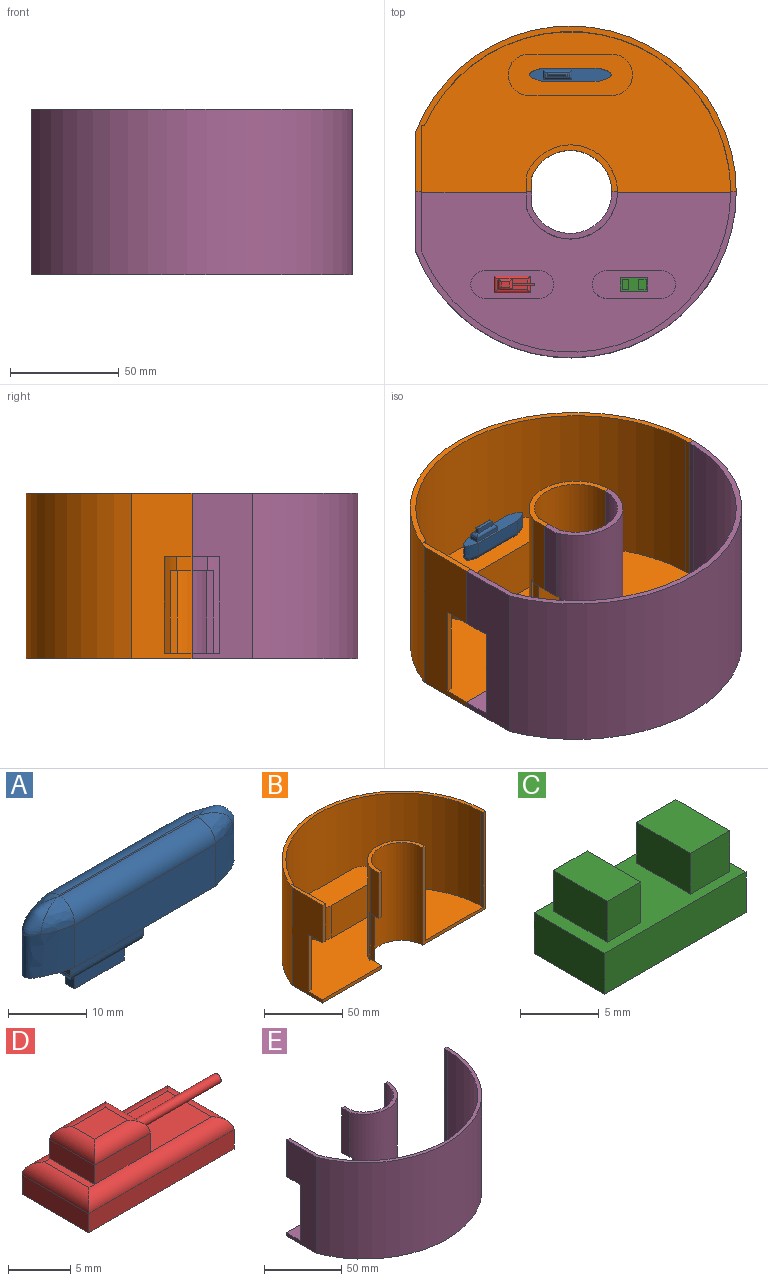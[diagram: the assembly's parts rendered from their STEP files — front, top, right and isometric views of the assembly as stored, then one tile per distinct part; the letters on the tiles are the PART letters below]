
ASSEMBLY  parts=5 mates=4
PART A: 32 faces, bbox 42x6.8x15.9 mm
  f0: plane 42.02x6.16mm, normal (0,0,-1), area 151.4mm2, adj f1,f2,f3,f4,f14,f15,f16,f17
  f1: extruded ~6.58x6.16mm, area 93mm2, adj f0,f2,f4,f6,f7,f9
  f2: plane 25.4x6.58mm, normal (0,-1,0), area 167.2mm2, adj f0,f1,f3,f8
  f3: extruded ~6.58x6.16mm, area 92.6mm2, adj f0,f2,f4,f10,f12,f13
  f4: plane 25.4x6.58mm, normal (0,1,0), area 167.2mm2, adj f0,f1,f3,f11
  f5: plane 25.67x0.28mm, normal (0,0,1), area 6.9mm2, adj f6,f8,f9,f10,f11,f13
  f6: bspline ~6.05x4.39mm, area 15.2mm2, adj f1,f5,f7,f8
  f7: bspline ~5.92x3.06mm, area 15.5mm2, adj f1,f6,f9
  f8: cylinder r=2.94mm len=25.4mm, axis (-1,0,0), area 115.7mm2, adj f2,f5,f6,f10
  f9: bspline ~5.92x4.35mm, area 15.1mm2, adj f1,f5,f7,f11
  f10: bspline ~5.89x4.34mm, area 15mm2, adj f3,f5,f8,f12
  f11: cylinder r=2.94mm len=25.4mm, axis (1,0,0), area 115.7mm2, adj f4,f5,f9,f13
  f12: bspline ~5.89x3.07mm, area 11.3mm2, adj f3,f10,f13
  f13: bspline ~7.54x4.77mm, area 15.1mm2, adj f3,f5,f11,f12
  f14: plane 4.16x1.91mm, normal (-1,0,0), area 7.9mm2, adj f0,f15,f17,f28
  f15: plane 13.17x1.91mm, normal (0,1,0), area 25.1mm2, adj f0,f14,f16,f30
  f16: plane 4.16x1.91mm, normal (1,0,0), area 7.9mm2, adj f0,f15,f17,f31
  f17: plane 13.17x1.91mm, normal (0,-1,0), area 25.1mm2, adj f0,f14,f16,f29
  f18: plane 10.63x1.62mm, normal (0,0,-1), area 2.9mm2, adj f19,f21,f22,f28,f29,f30,f31
  f19: plane 2.41x1.64mm, normal (-1,0,0), area 4mm2, adj f18,f20,f22,f24,f30
  f20: plane 9.02x2.41mm, normal (0,1,0), area 21.8mm2, adj f19,f21,f26,f30
  f21: plane 2.41x1.64mm, normal (1,0,0), area 4mm2, adj f18,f20,f22,f27,f30
  f22: plane 9.02x2.41mm, normal (0,-1,0), area 21.8mm2, adj f18,f19,f21,f25
  f23: plane 7.49x0.12mm, normal (0,0,-1), area 0.9mm2, adj f24,f25,f26,f27
  f24: plane 1.64x0.76mm, normal (-0.71,0,-0.71), area 0.9mm2, adj f19,f23,f25,f26
  f25: plane 9.02x0.76mm, normal (0,-0.71,-0.71), area 8.9mm2, adj f22,f23,f24,f27
  f26: plane 9.02x0.76mm, normal (0,0.71,-0.71), area 8.9mm2, adj f20,f23,f24,f27
  f27: plane 1.64x0.76mm, normal (0.71,0,-0.71), area 0.9mm2, adj f21,f23,f25,f26
  f28: cylinder r=1.27mm len=4.16mm, axis (0,-1,0), area 5.8mm2, adj f14,f18,f29,f30
  f29: cylinder r=1.27mm len=13.17mm, axis (1,0,0), area 23.7mm2, adj f17,f18,f28,f31
  f30: cylinder r=1.27mm len=13.17mm, axis (-1,0,0), area 23.9mm2, adj f15,f18,f19,f20,f21,f28,f31
  f31: cylinder r=1.27mm len=4.16mm, axis (0,1,0), area 5.8mm2, adj f16,f18,f29,f30
PART B: 32 faces, bbox 147.2x76.2x76.2 mm
  f0: plane 147.23x76.2mm, normal (0,0,1), area 593.9mm2, adj f2,f5,f10,f11,f12,f16,f28,f29
  f1: plane 73.66x0.15mm, normal (0,1,0), area 11mm2, adj f4,f6,f8,f31
  f2: plane 29.21x2.54mm, normal (0,-1,0), area 74.2mm2, adj f0,f12,f16,f18
  f3: plane 53.25x2.54mm, normal (0,-1,0), area 135.3mm2, adj f6,f7,f12,f15
  f4: plane 41.9x21.59mm, normal (0,0,1), area 161.9mm2, adj f1,f8,f9,f10,f13,f14,f17,f31
  f5: cylinder r=73.66mm len=140.67mm, axis (0,0,-1), area 14543.8mm2, adj f0,f6,f28,f29
  f6: plane 144.69x73.66mm, normal (0,0,1), area 6750.3mm2, adj f1,f3,f5,f7,f8,f10,f12,f16
  f7: plane 6.86x2.54mm, normal (1,0,0), area 17.4mm2, adj f3,f6,f9,f15
  f8: cylinder r=21.59mm len=73.66mm, axis (0,0,-1), area 4146.6mm2, adj f1,f4,f6,f17,f20,f21
  f9: cylinder r=19.05mm len=76.2mm, axis (0,0,-1), area 4025.6mm2, adj f4,f7,f10,f14,f15,f22
  f10: plane 76.2x57.15mm, normal (0,-1,0), area 519.4mm2, adj f0,f4,f6,f9,f11,f15,f30,f31
  f11: cylinder r=76.2mm len=147.23mm, axis (0,0,-1), area 16089.2mm2, adj f0,f10,f12,f15
  f12: plane 76.2x27.6mm, normal (-1,0,0), area 1538.8mm2, adj f0,f2,f3,f6,f11,f15,f18,f19
  f13: plane 35.56x2.54mm, normal (0,-1,0), area 90.3mm2, adj f4,f14,f17,f20
  f14: plane 35.56x6.86mm, normal (1,0,0), area 243.9mm2, adj f4,f9,f13,f20
  f15: plane 147.23x76.2mm, normal (0,0,-1), area 8460.7mm2, adj f3,f7,f9,f10,f11,f12
  f16: plane 73.66x30.48mm, normal (1,0,0), area 1680.6mm2, adj f0,f2,f6,f18,f19,f28
  f17: plane 35.56x7.32mm, normal (-1,0,0), area 260.2mm2, adj f4,f8,f13,f20
  f18: plane 12.7x2.54mm, normal (0,0,-1), area 32.3mm2, adj f2,f12,f16,f19
  f19: plane 44.45x2.54mm, normal (0,-1,0), area 112.9mm2, adj f6,f12,f16,f18
  f20: plane 10.01x2.54mm, normal (0,0,-1), area 23.9mm2, adj f8,f13,f14,f17,f21,f22
  f21: plane 38.1x1.36mm, normal (0,-1,0), area 51.7mm2, adj f6,f8,f20,f22
  f22: plane 38.1x3.15mm, normal (-1,0,0), area 120mm2, adj f6,f9,f20,f21
  f23: cylinder r=9.53mm len=25.4mm, axis (0,0,-1), area 760.1mm2, adj f6,f24,f26,f27
  f24: plane 38.1x25.4mm, normal (0,-1,0), area 967.7mm2, adj f6,f23,f25,f27
  f25: cylinder r=9.53mm len=25.4mm, axis (0,0,-1), area 760.1mm2, adj f6,f24,f26,f27
  f26: plane 38.1x25.4mm, normal (0,1,0), area 967.7mm2, adj f6,f23,f25,f27
  f27: plane 57.15x19.05mm, normal (0,0,1), area 1010.8mm2, adj f23,f24,f25,f26
  f28: plane 73.66x1.43mm, normal (0,-1,0), area 105.1mm2, adj f0,f5,f6,f16
  f29: plane 73.66x0.04mm, normal (0,-1,0), area 3.2mm2, adj f0,f5,f6,f30
  f30: plane 73.66x2.54mm, normal (-1,0,0), area 187.1mm2, adj f0,f6,f10,f29
  f31: plane 73.66x2.54mm, normal (1,0,0), area 187.1mm2, adj f1,f4,f6,f10
PART C: 16 faces, bbox 12.7x6.4x6.4 mm
  f0: plane 12.7x3.18mm, normal (0,1,0), area 40.3mm2, adj f1,f3,f4,f5
  f1: plane 6.35x3.18mm, normal (-1,0,0), area 20.2mm2, adj f0,f2,f4,f5
  f2: plane 12.7x3.18mm, normal (0,-1,0), area 40.3mm2, adj f1,f3,f4,f5
  f3: plane 6.35x3.18mm, normal (1,0,0), area 20.2mm2, adj f0,f2,f4,f5
  f4: plane 12.7x6.35mm, normal (0,0,1), area 49mm2, adj f0,f1,f2,f3,f7,f8,f9,f10
  f5: plane 12.7x6.35mm, normal (0,0,-1), area 80.6mm2, adj f0,f1,f2,f3
  f6: plane 4.83x3.03mm, normal (0,0,1), area 14.6mm2, adj f7,f8,f9,f10
  f7: plane 4.83x3.18mm, normal (1,0,0), area 15.3mm2, adj f4,f6,f8,f10
  f8: plane 3.18x3.03mm, normal (0,-1,0), area 9.6mm2, adj f4,f6,f7,f9
  f9: plane 4.83x3.18mm, normal (-1,0,0), area 15.3mm2, adj f4,f6,f8,f10
  f10: plane 3.18x3.03mm, normal (0,1,0), area 9.6mm2, adj f4,f6,f7,f9
  f11: plane 4.83x3.53mm, normal (0,0,1), area 17mm2, adj f12,f13,f14,f15
  f12: plane 4.83x3.18mm, normal (1,0,0), area 15.3mm2, adj f4,f11,f13,f15
  f13: plane 3.53x3.18mm, normal (0,-1,0), area 11.2mm2, adj f4,f11,f12,f14
  f14: plane 4.83x3.18mm, normal (-1,0,0), area 15.3mm2, adj f4,f11,f13,f15
  f15: plane 3.53x3.18mm, normal (0,1,0), area 11.2mm2, adj f4,f11,f12,f14
PART D: 22 faces, bbox 18.4x7.6x6.4 mm
  f0: plane 5.04x0.62mm, normal (0,0,1), area 3.1mm2, adj f10,f16,f17,f19
  f1: plane 16.51x1.89mm, normal (0,1,0), area 31.2mm2, adj f2,f4,f6,f16
  f2: plane 7.62x1.89mm, normal (-1,0,0), area 14.4mm2, adj f1,f3,f6,f17
  f3: plane 16.51x1.89mm, normal (0,-1,0), area 31.2mm2, adj f2,f4,f6,f19
  f4: plane 7.62x1.89mm, normal (1,0,0), area 14.4mm2, adj f1,f3,f6,f18
  f5: plane 6.97x5.04mm, normal (0,0,1), area 35.1mm2, adj f8,f16,f18,f19
  f6: plane 16.51x7.62mm, normal (0,0,-1), area 125.8mm2, adj f1,f2,f3,f4
  f7: plane 3.77x2.5mm, normal (0,0,1), area 9.5mm2, adj f12,f13,f14,f15
  f8: plane 5.08x1.89mm, normal (1,0,0), area 9mm2, adj f5,f9,f11,f14,f16,f19,f20
  f9: plane 6.35x1.89mm, normal (0,-1,0), area 12mm2, adj f8,f10,f15,f19
  f10: plane 5.08x1.89mm, normal (-1,0,0), area 9.6mm2, adj f0,f9,f11,f13,f16,f19
  f11: plane 6.35x1.89mm, normal (0,1,0), area 12mm2, adj f8,f10,f12,f16
  f12: cylinder r=1.29mm len=6.35mm, axis (1,0,0), area 11mm2, adj f7,f11,f13,f14
  f13: cylinder r=1.29mm len=5.08mm, axis (0,1,0), area 8.4mm2, adj f7,f10,f12,f15
  f14: cylinder r=1.29mm len=5.08mm, axis (0,-1,0), area 8.4mm2, adj f7,f8,f12,f15
  f15: cylinder r=1.29mm len=6.35mm, axis (-1,0,0), area 11mm2, adj f7,f9,f13,f14
  f16: cylinder r=1.29mm len=16.51mm, axis (1,0,0), area 31.4mm2, adj f0,f1,f5,f8,f10,f11,f17,f18
  f17: cylinder r=1.29mm len=7.62mm, axis (0,1,0), area 13.5mm2, adj f0,f2,f16,f19
  f18: cylinder r=1.29mm len=7.62mm, axis (0,-1,0), area 13.5mm2, adj f4,f5,f16,f19
  f19: cylinder r=1.29mm len=16.51mm, axis (-1,0,0), area 31.4mm2, adj f0,f3,f5,f8,f9,f10,f17,f18
  f20: cylinder r=0.44mm len=10.16mm, axis (-1,0,0), area 28.4mm2, adj f8,f21
  f21: plane 0.89x0.89mm, normal (1,0,0), area 0.6mm2, adj f20
PART E: 39 faces, bbox 147.2x76.2x76.2 mm
  f0: plane 41.9x21.59mm, normal (0,0,1), area 161.9mm2, adj f1,f2,f9,f10,f11,f14,f15,f37
  f1: plane 73.66x0.15mm, normal (0,-1,0), area 11mm2, adj f0,f5,f14,f37
  f2: plane 35.56x2.54mm, normal (0,1,0), area 90.3mm2, adj f0,f11,f15,f21
  f3: plane 29.21x2.54mm, normal (0,1,0), area 74.2mm2, adj f4,f8,f16,f19
  f4: plane 147.23x76.2mm, normal (0,0,1), area 596.2mm2, adj f3,f8,f9,f12,f16,f17,f36,f38
  f5: plane 144.69x73.66mm, normal (0,0,1), area 6858.7mm2, adj f1,f6,f7,f8,f9,f14,f16,f17
  f6: plane 6.86x2.54mm, normal (1,0,0), area 17.4mm2, adj f5,f7,f10,f13
  f7: plane 53.25x2.54mm, normal (0,1,0), area 135.3mm2, adj f5,f6,f8,f13
  f8: plane 76.2x27.6mm, normal (-1,0,0), area 1538.8mm2, adj f3,f4,f5,f7,f12,f13,f18,f19
  f9: plane 76.2x57.15mm, normal (0,1,0), area 519.4mm2, adj f0,f4,f5,f10,f12,f13,f36,f37
  f10: cylinder r=19.05mm len=76.2mm, axis (0,0,-1), area 4025.6mm2, adj f0,f6,f9,f11,f13,f20
  f11: plane 35.56x6.86mm, normal (1,0,0), area 243.9mm2, adj f0,f2,f10,f21
  f12: cylinder r=76.2mm len=147.23mm, axis (0,0,-1), area 16089.2mm2, adj f4,f8,f9,f13
  f13: plane 147.23x76.2mm, normal (0,0,-1), area 8460.7mm2, adj f6,f7,f8,f9,f10,f12
  f14: cylinder r=21.59mm len=73.66mm, axis (0,0,-1), area 4146.6mm2, adj f0,f1,f5,f15,f21,f22
  f15: plane 35.56x7.32mm, normal (-1,0,0), area 260.2mm2, adj f0,f2,f14,f21
  f16: plane 73.66x27.12mm, normal (1,0,0), area 1433.3mm2, adj f3,f4,f5,f17,f18,f19
  f17: cylinder r=73.66mm len=142.1mm, axis (0,0,-1), area 14812.5mm2, adj f4,f5,f16,f38
  f18: plane 44.45x2.54mm, normal (0,1,0), area 112.9mm2, adj f5,f8,f16,f19
  f19: plane 12.7x2.54mm, normal (0,0,-1), area 32.3mm2, adj f3,f8,f16,f18
  f20: plane 38.1x3.15mm, normal (-1,0,0), area 120mm2, adj f5,f10,f21,f22
  f21: plane 10.01x2.54mm, normal (0,0,-1), area 23.9mm2, adj f2,f11,f14,f15,f20,f22
  f22: plane 38.1x1.36mm, normal (0,1,0), area 51.7mm2, adj f5,f14,f20,f21
  f23: plane 25.4x25.4mm, normal (0,-1,0), area 645.1mm2, adj f5,f24,f26,f27
  f24: cylinder r=6.35mm len=25.4mm, axis (0,0,-1), area 506.7mm2, adj f5,f23,f25,f27
  f25: plane 25.4x25.4mm, normal (0,1,0), area 645.1mm2, adj f5,f24,f26,f27
  f26: cylinder r=6.35mm len=25.4mm, axis (0,0,-1), area 506.7mm2, adj f5,f23,f25,f27
  f27: plane 38.1x12.7mm, normal (0,0,1), area 449.2mm2, adj f23,f24,f25,f26
  f28: cylinder r=6.35mm len=25.4mm, axis (0,0,-1), area 509.8mm2, adj f5,f29,f34,f35
  f29: plane 25.52x25.4mm, normal (0,-1,0), area 648.3mm2, adj f5,f28,f30,f35
  f30: plane 25.4x0mm, normal (1,0,0), area 0mm2, adj f5,f29,f31,f35
  f31: cylinder r=6.35mm len=25.4mm, axis (0,0,-1), area 500.5mm2, adj f5,f30,f32,f35
  f32: plane 25.4x0mm, normal (1,0,0), area 0mm2, adj f5,f31,f33,f35
  f33: plane 25.64x25.4mm, normal (0,1,0), area 651.4mm2, adj f5,f32,f34,f35
  f34: plane 25.4x0mm, normal (-1,0,0), area 0mm2, adj f5,f28,f33,f35
  f35: plane 38.22x12.7mm, normal (0,0,1), area 450.8mm2, adj f28,f29,f30,f31,f32,f33,f34
  f36: plane 73.66x2.54mm, normal (-1,0,0), area 187.1mm2, adj f4,f5,f9,f38
  f37: plane 73.66x2.54mm, normal (1,0,0), area 187.1mm2, adj f0,f1,f5,f9
  f38: plane 73.66x0.04mm, normal (0,1,0), area 3.2mm2, adj f4,f5,f17,f36
PLACE A rot(axis=(1,0,0),180deg) t=(13.15,75.23,57.71)mm
PLACE B t=(-4.7,-0.55,20.25)mm
PLACE C t=(65.89,-81.59,48.19)mm
PLACE D t=(-7.07,-72.54,48.19)mm
PLACE E t=(-4.7,-0.55,20.25)mm
MATE fastened D.f6 <-> E.f27  axis (0,0,-1) through (-31.44,-43,48.19)mm
MATE fastened E.f10 <-> B.f5  axis (0,0,-1) through (-4.7,-0.55,58.35)mm
MATE fastened A.f5 <-> B.f27  axis (0,0,-1) through (-4.7,53.33,48.19)mm
MATE fastened C.f5 <-> E.f35  axis (0,0,-1) through (24.46,-43,48.19)mm
